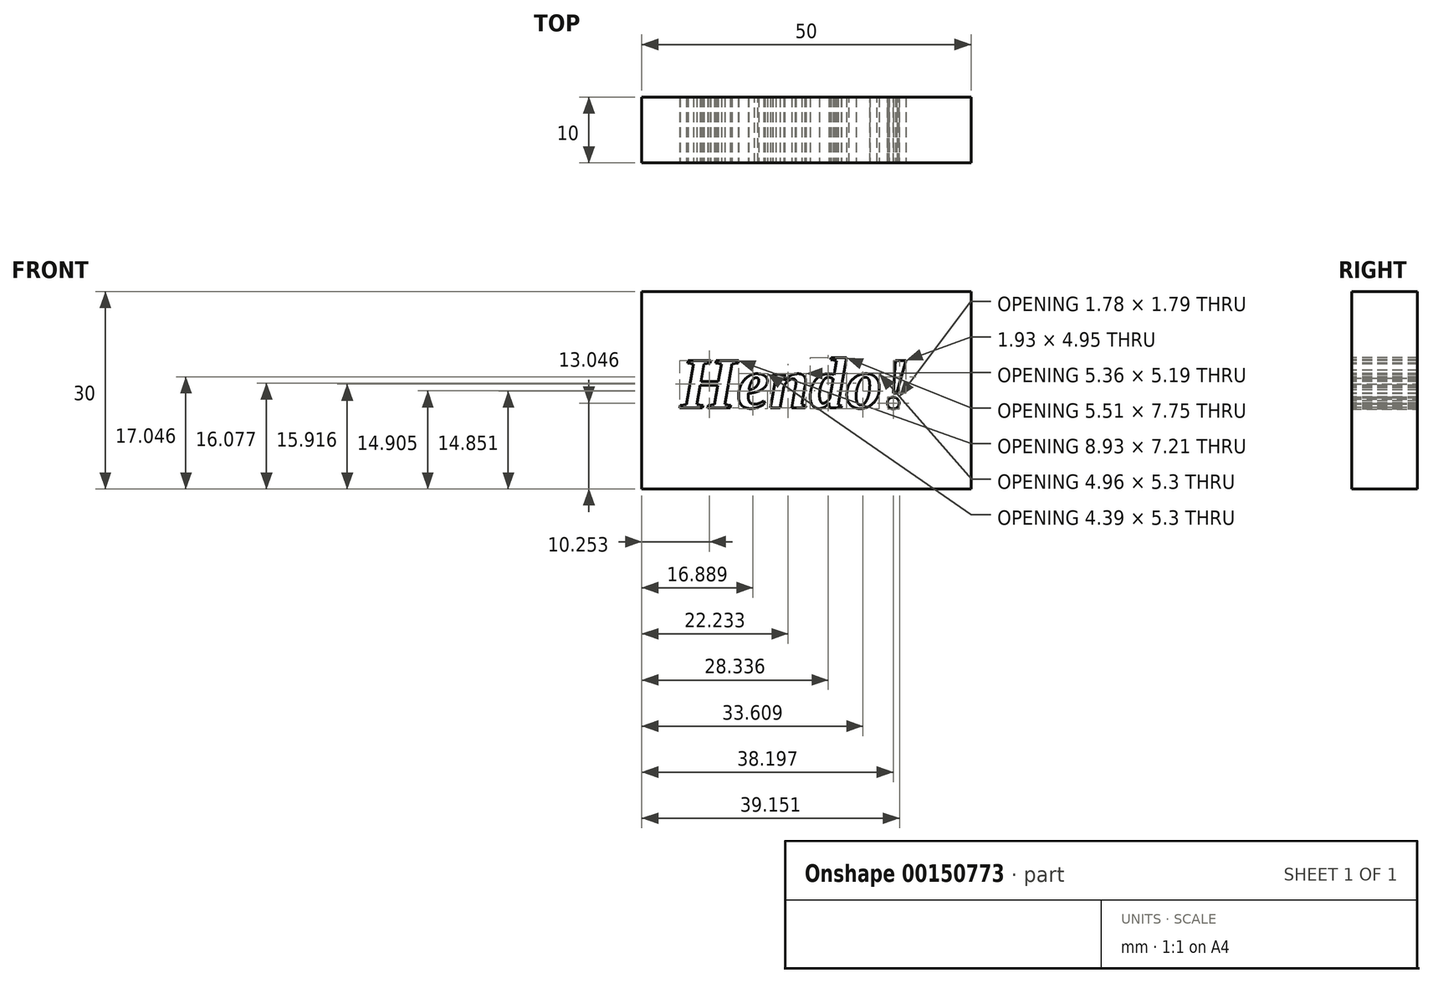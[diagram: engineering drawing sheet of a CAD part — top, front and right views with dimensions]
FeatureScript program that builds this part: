
annotation { "Feature Type Name" : "Feature", "Feature Type Description" : "" }
export const myFeature = defineFeature(function(context is Context, id is Id, definition is map)
    precondition{}
    {
        {
            var Q0;
            Q0=qCreatedBy(makeId("Front.planeOp"),FACE);
            var sketch = newSketch(context, id + "F0", { "sketchPlane" : qUnion([Q0])});
            skLineSegment(sketch, "E0.bottom", {"start": v(-9.14, 14.33) * mm, "end": v(40.86, 14.33) * mm});
            skLineSegment(sketch, "E0.top", {"start": v(-9.14, -15.67) * mm, "end": v(40.86, -15.67) * mm});
            skLineSegment(sketch, "E0.left", {"start": v(-9.14, 14.33) * mm, "end": v(-9.14, -15.67) * mm});
            skLineSegment(sketch, "E0.right", {"start": v(40.86, 14.33) * mm, "end": v(40.86, -15.67) * mm});
            skSolve(sketch);
        }
        {
            var Q0;
            Q0=makeQuery(id+"F0.imprint","IMPRINT",FACE,{"disambiguationData":[TD([[makeQuery(id+"F0.imprint","IMPRINT",EDGE,{"derivedFrom":sQuery(id+"F0.wireOp",EDGE,"E0.bottom")}),-1.0]])]});
            extrude(context, id + "F1", {"entities" : qUnion([Q0]), "depth" : 10 * mm});
        }
        {
            var Q0;
            Q0=makeQuery(id+"F1.opExtrude","CAP_FACE",FACE,{"disambiguationData":[OSD([sQuery(id+"F0.wireOp",EDGE,"E0.bottom"),sQuery(id+"F0.wireOp",EDGE,"E0.top"),sQuery(id+"F0.wireOp",EDGE,"E0.left"),sQuery(id+"F0.wireOp",EDGE,"E0.right")])],"isStart":false});
            var sketch = newSketch(context, id + "F2", { "sketchPlane" : qUnion([Q0])});
            skText(sketch, "E1", { "text": "Hendo!", "fontName": "Tinos-BoldItalic.ttf"});
            const initialGuessF2  = {"E1": [-0.00327, -0.00336, 1, 0, 0.00793]};
            skSetInitialGuess(sketch, initialGuessF2);
            skSolve(sketch);
        }
        {
            var Q0;
            Q0 = qSketchRegion(id + "F2", true);
            extrude(context, id + "F3", {"entities" : qUnion([Q0]), "operationType" : NewBodyOperationType.REMOVE, "oppositeDirection" : true, "depth" : 10 * mm});
        }
    });
